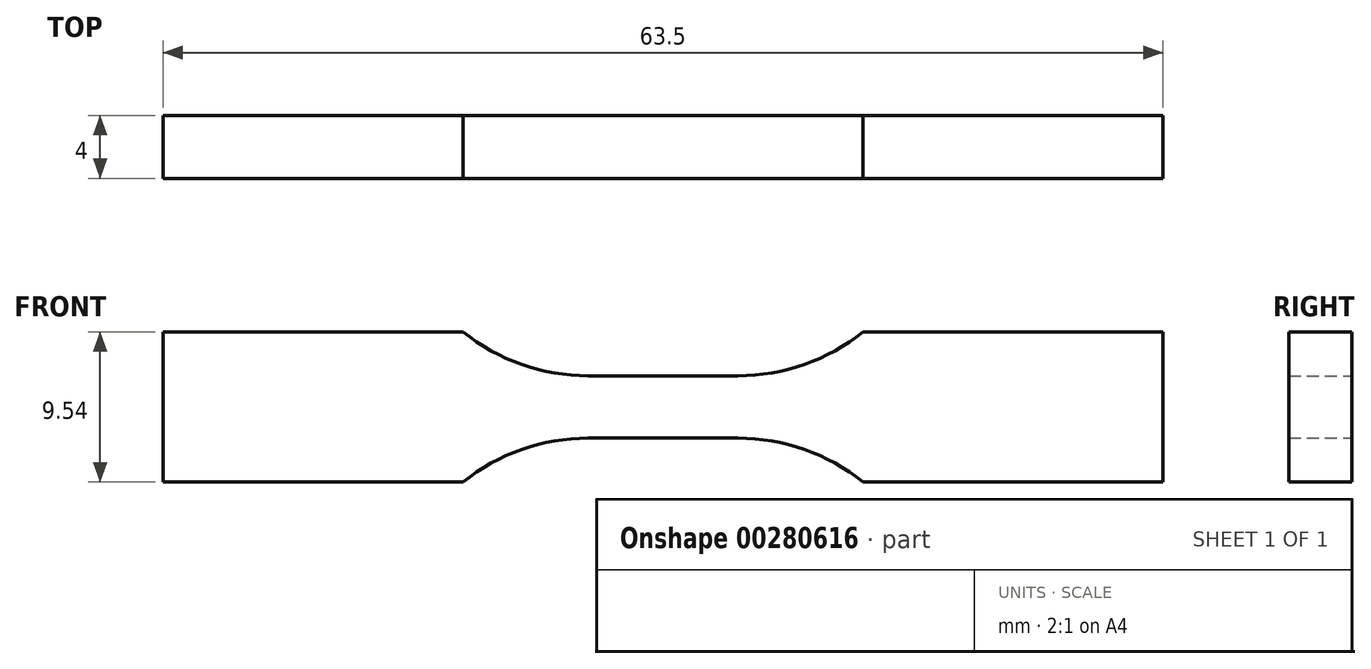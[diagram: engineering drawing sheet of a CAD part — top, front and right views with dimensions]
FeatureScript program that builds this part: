
annotation { "Feature Type Name" : "Feature", "Feature Type Description" : "" }
export const myFeature = defineFeature(function(context is Context, id is Id, definition is map)
    precondition{}
    {
        {
            var Q0;
            Q0=qCreatedBy(makeId("Front.planeOp"),FACE);
            var sketch = newSketch(context, id + "F0", { "sketchPlane" : qUnion([Q0])});
            skLineSegment(sketch, "E0", {"start": v(0, 1.98) * mm, "end": v(4.77, 1.98) * mm});
            skArc(sketch, "E1", {"start": v(4.76, 1.98) * mm, "mid": v(8.97, 2.7) * mm, "end": v(12.7, 4.76) * mm});
            skLineSegment(sketch, "E2", {"start": v(12.7, 4.77) * mm, "end": v(31.75, 4.77) * mm});
            skLineSegment(sketch, "E3", {"start": v(31.75, 4.77) * mm, "end": v(31.75, 0) * mm});
            skLineSegment(sketch, "E4.MirrorCS", {"start": v(0, -1.98) * mm, "end": v(4.77, -1.98) * mm});
            skLineSegment(sketch, "E5.MirrorCS", {"start": v(12.7, -4.77) * mm, "end": v(31.75, -4.77) * mm});
            skArc(sketch, "E6.MirrorCS", {"start": v(4.76, -1.98) * mm, "mid": v(8.97, -2.7) * mm, "end": v(12.7, -4.76) * mm});
            skLineSegment(sketch, "E7.MirrorCS", {"start": v(31.75, -4.77) * mm, "end": v(31.75, 0) * mm});
            skLineSegment(sketch, "E8.MirrorCS", {"start": v(0, 1.98) * mm, "end": v(-4.77, 1.98) * mm});
            skArc(sketch, "E9.MirrorCS", {"start": v(-4.76, 1.98) * mm, "mid": v(-8.97, 2.7) * mm, "end": v(-12.7, 4.76) * mm});
            skLineSegment(sketch, "E10.MirrorCS", {"start": v(-12.7, 4.77) * mm, "end": v(-31.75, 4.77) * mm});
            skLineSegment(sketch, "E11.MirrorCS", {"start": v(-31.75, 4.77) * mm, "end": v(-31.75, 0) * mm});
            skLineSegment(sketch, "E12.MirrorCS", {"start": v(-31.75, -4.77) * mm, "end": v(-31.75, 0) * mm});
            skLineSegment(sketch, "E13.MirrorCS", {"start": v(-12.7, -4.77) * mm, "end": v(-31.75, -4.77) * mm});
            skArc(sketch, "E14.MirrorCS", {"start": v(-4.76, -1.98) * mm, "mid": v(-8.97, -2.7) * mm, "end": v(-12.7, -4.76) * mm});
            skLineSegment(sketch, "E15.MirrorCS", {"start": v(0, -1.98) * mm, "end": v(-4.77, -1.98) * mm});
            skSolve(sketch);
        }
        {
            var Q0;
            Q0 = qSketchRegion(id + "F0", true);
            extrude(context, id + "F1", {"entities" : qUnion([Q0]), "endBound" : BoundingType.SYMMETRIC, "depth" : 4 * mm});
        }
    });
